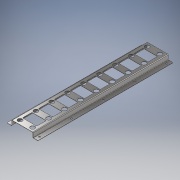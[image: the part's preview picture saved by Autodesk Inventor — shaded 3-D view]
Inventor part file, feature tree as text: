
AUTODESK INVENTOR PART (.ipt)
format: ipt  version: 2021 (Build 250183000, 183)  size: 382,976 bytes
history: native  units: mm
features: other x5, sketch x4, sheet_metal_op x3, pattern_linear x3, fillet x2
ambient origin geometry x8: Origin, YZ Plane, XZ Plane, XY Plane, X Axis, Y Axis, Z Axis, Center Point
bodies: Solid1 (feature_tree)
feature tree (17):
  sheet_metal_op  "Contour Flange1"
  fillet  "Fillet1"  Radius=30.0mm
  pattern_linear  "Rectangular Pattern1"  Count1=3  [1 undecoded]
  pattern_linear  "Rectangular Pattern2"  Spacing1=3.0mm  [1 undecoded]
  fillet  "Fillet2"  Radius=1.5mm
  pattern_linear  "Rectangular Pattern3"  Count1=85  [1 undecoded]
  sketch  "Sketch1"  dims[d2=135.0mm]
  other  "Plate1"
  sheet_metal_op  "Bend1"
  sheet_metal_op  "Corner1"
  sketch  "Sketch2"  dims[d3=1.5mm]
  sketch  "Sketch3"  dims[d4=1.5mm]
  sketch  "Sketch5"  dims[d5=0.75mm d6=3.0mm d7=1.5mm d8=850.0mm d9=2.0mm d10=0.5mm d11=6.0mm d12=1.5mm d13=1.5mm d14=5.0mm d15=80.0mm d16=28.0mm d17=1.5mm d18=0.0mm d19=90.0mm d21=100.0mm d22=10.0mm d23=165.0mm d24=1.5mm d25=0.0mm d26=50.0mm d28=200.0mm d42=5.0mm d43=20.0mm d44=20.0mm d45=5.0mm d46=1.5mm d47=0.0mm d48=5.0mm d49=80.0mm d51=100.0mm]
  other  "Cut1"
  other  "Cut2"
  other  "Cut4"
  other  "Definition1"
note: 3 required parameter values undecoded (feature->parameter linkage not recoverable at this tier; creation-order binding heuristic only, values carry confidence <= 0.55)
